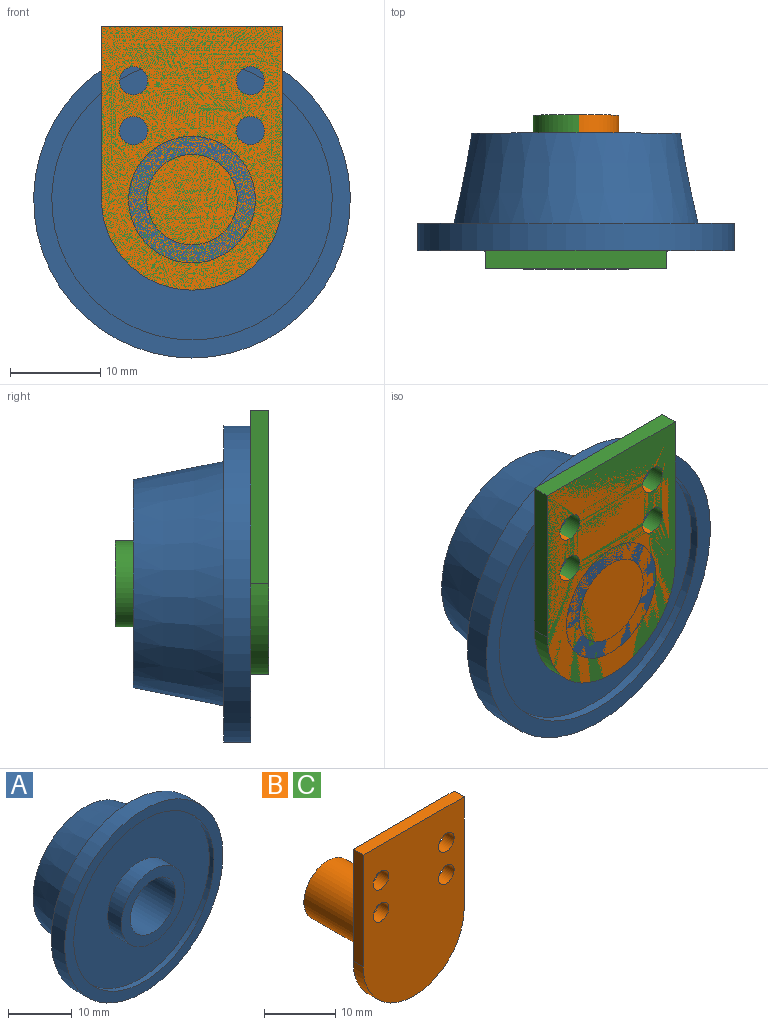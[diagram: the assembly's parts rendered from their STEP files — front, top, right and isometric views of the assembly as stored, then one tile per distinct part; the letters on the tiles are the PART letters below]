
ASSEMBLY  parts=3 mates=1
PART A: 12 faces, bbox 35x15x35 mm
  f0: cone r=11.5mm half-angle=11.3deg, axis (0,-1,0), area 801mm2, adj f1,f11
  f1: plane 35x35mm, normal (0,1,0), area 389.6mm2, adj f0,f2
  f2: cylinder r=17.5mm len=35mm, axis (0,-1,0), area 329.9mm2, adj f1,f3
  f3: plane 35x35mm, normal (0,-1,0), area 207.3mm2, adj f2,f4
  f4: cylinder r=15.5mm len=31mm, axis (0,-1,0), area 97.4mm2, adj f3,f5
  f5: plane 31x31mm, normal (0,-1,0), area 600.8mm2, adj f4,f6
  f6: cylinder r=7mm len=14mm, axis (0,-1,0), area 131.9mm2, adj f5,f7
  f7: plane 14x14mm, normal (0,-1,0), area 75.4mm2, adj f6,f8
  f8: cylinder r=5mm len=13mm, axis (0,-1,0), area 408.4mm2, adj f7,f9
  f9: plane 16x16mm, normal (0,1,0), area 122.5mm2, adj f8,f10
  f10: cone r=8mm half-angle=36.9deg, axis (0,1,0), area 137.4mm2, adj f9,f11
  f11: plane 23x23mm, normal (0,1,0), area 131.9mm2, adj f0,f10
PART B: 12 faces, bbox 20x17x29.2 mm
  f0: cylinder r=4.75mm len=15mm, axis (0,-1,0), area 447.7mm2, adj f1,f10
  f1: plane 9.5x9.5mm, normal (0,1,0), area 70.9mm2, adj f0
  f2: plane 19.19x2mm, normal (-1,0,0), area 38.4mm2, adj f3,f8,f10,f11
  f3: cylinder r=10mm len=20mm, axis (0,-1,0), area 62.8mm2, adj f2,f4,f10,f11
  f4: plane 19.19x2mm, normal (1,0,0), area 38.4mm2, adj f3,f8,f10,f11
  f5: cylinder r=1.55mm len=3.1mm, axis (0,-1,0), area 19.5mm2, adj f10,f11
  f6: cylinder r=1.55mm len=3.1mm, axis (0,-1,0), area 19.5mm2, adj f10,f11
  f7: cylinder r=1.55mm len=3.1mm, axis (0,-1,0), area 19.5mm2, adj f10,f11
  f8: plane 20x2mm, normal (0,0,1), area 40mm2, adj f2,f4,f10,f11
  f9: cylinder r=1.55mm len=3.1mm, axis (0,-1,0), area 19.5mm2, adj f10,f11
  f10: plane 29.19x20mm, normal (0,1,0), area 439.8mm2, adj f0,f2,f3,f4,f5,f6,f7,f8
  f11: plane 29.19x20mm, normal (0,-1,0), area 510.6mm2, adj f2,f3,f4,f5,f6,f7,f8,f9
PART C: same geometry as B
PLACE A t=(-8.4,-14.83,-8.06)mm
PLACE B t=(-8.4,-14.83,-8.06)mm
PLACE C t=(-8.4,-14.83,-8.06)mm
MATE cylindrical A.f0 <-> C.f3  axis (0,-1,0) through (-8.4,-14.83,-8.06)mm
